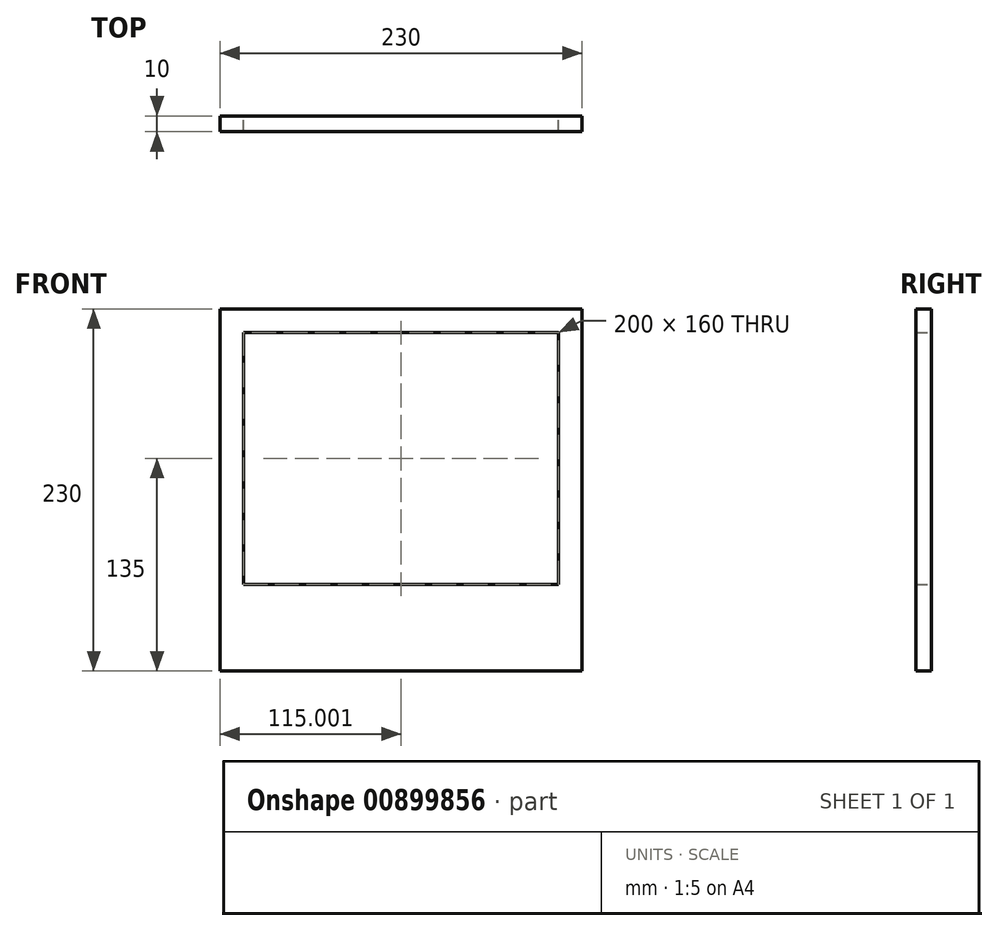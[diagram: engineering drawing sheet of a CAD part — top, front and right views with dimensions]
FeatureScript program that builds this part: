
annotation { "Feature Type Name" : "Feature", "Feature Type Description" : "" }
export const myFeature = defineFeature(function(context is Context, id is Id, definition is map)
    precondition{}
    {
        {
            var Q0;
            Q0=qCreatedBy(makeId("Front.planeOp"),FACE);
            var sketch = newSketch(context, id + "F0", { "sketchPlane" : qUnion([Q0])});
            skLineSegment(sketch, "E0", {"start": v(-114.99, -15) * mm, "end": v(115.01, -15) * mm});
            skLineSegment(sketch, "E1", {"start": v(115.01, -15) * mm, "end": v(115.01, 175) * mm});
            skLineSegment(sketch, "E2", {"start": v(115.01, 175) * mm, "end": v(-114.99, 175) * mm});
            skLineSegment(sketch, "E3", {"start": v(-114.99, -15) * mm, "end": v(-114.99, -55) * mm});
            skLineSegment(sketch, "E4", {"start": v(-114.99, -55) * mm, "end": v(115.01, -55) * mm});
            skLineSegment(sketch, "E5", {"start": v(115.01, -55) * mm, "end": v(115.01, -15) * mm});
            skLineSegment(sketch, "E6", {"start": v(-114.99, 175) * mm, "end": v(-114.99, -15) * mm});
            skLineSegment(sketch, "E7", {"start": v(-99.99, 160) * mm, "end": v(-99.99, 0) * mm});
            skLineSegment(sketch, "E8", {"start": v(-99.99, 0) * mm, "end": v(100.01, 0) * mm});
            skLineSegment(sketch, "E9", {"start": v(100.01, 0) * mm, "end": v(100.01, 160) * mm});
            skLineSegment(sketch, "E10", {"start": v(100.01, 160) * mm, "end": v(-99.99, 160) * mm});
            skSolve(sketch);
        }
        {
            var Q0;
            Q0=makeQuery(id+"F0.imprint","IMPRINT",FACE,{"disambiguationData":[TD([[makeQuery(id+"F0.imprint","IMPRINT",EDGE,{"derivedFrom":sQuery(id+"F0.wireOp",EDGE,"EnDeeEoz-1aXI-aVQo-01ff-V3cURg8vh1G4")}),-1.0]])]});
            var Q1;
            Q1=makeQuery(id+"F0.imprint","IMPRINT",FACE,{"disambiguationData":[TD([[makeQuery(id+"F0.imprint","IMPRINT",EDGE,{"derivedFrom":sQuery(id+"F0.wireOp",EDGE,"E0")}),-1.0]])]});
            var Q2;
            Q2=makeQuery(id+"F0.imprint","IMPRINT",FACE,{"disambiguationData":[TD([[makeQuery(id+"F0.imprint","IMPRINT",EDGE,{"derivedFrom":sQuery(id+"F0.wireOp",EDGE,"E0")}),1.0]])]});
            extrude(context, id + "F1", {"entities" : qUnion([Q0, Q1, Q2]), "depth" : 10 * mm, "offsetDistance" : 25 * mm});
        }
    });
